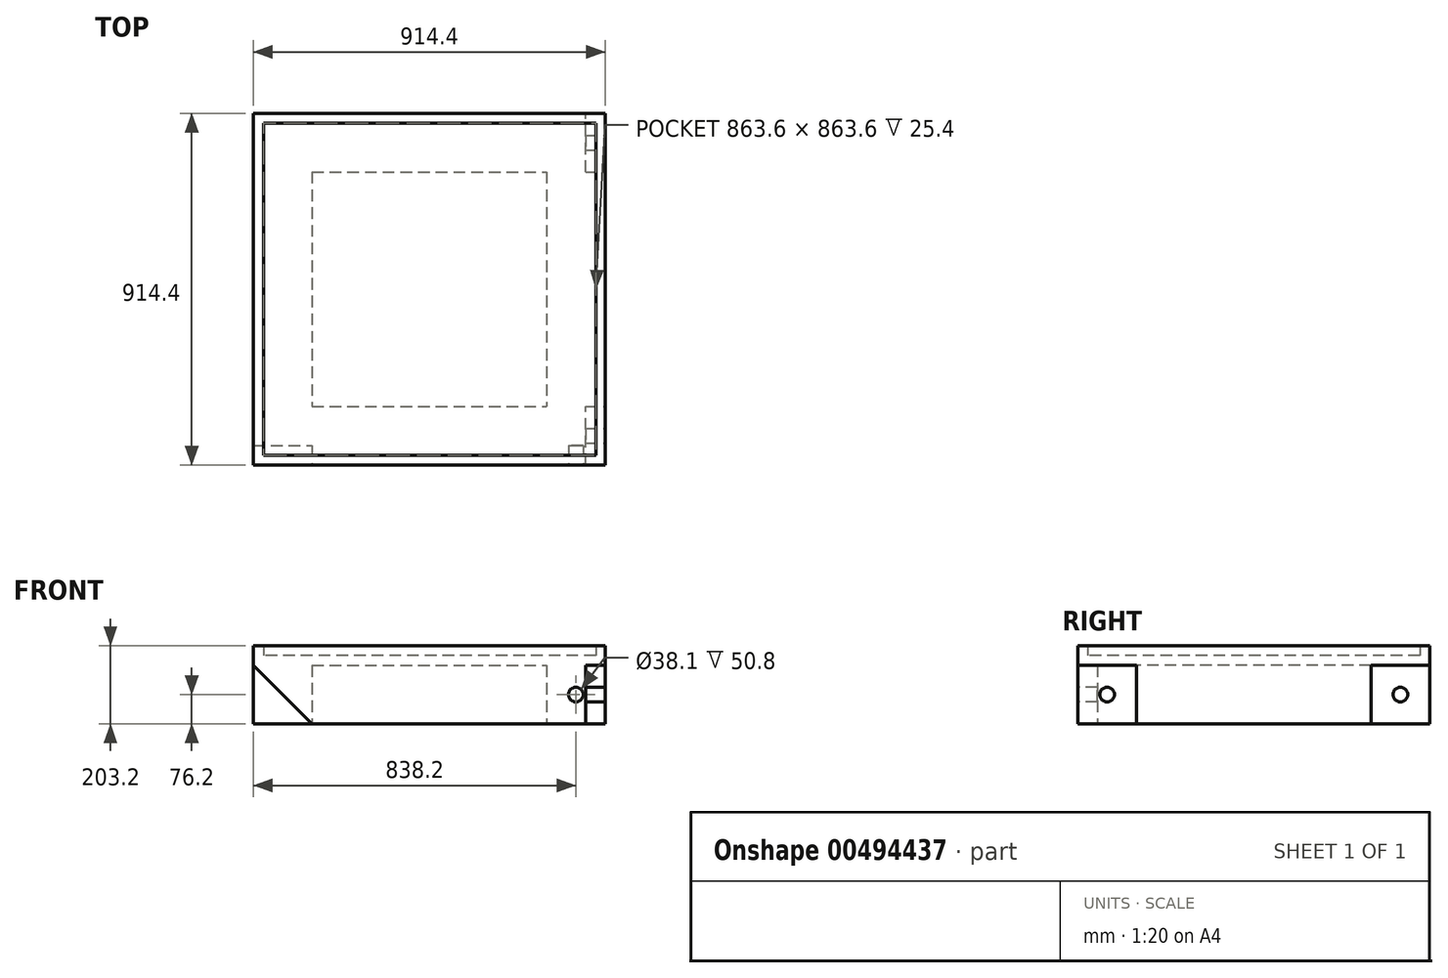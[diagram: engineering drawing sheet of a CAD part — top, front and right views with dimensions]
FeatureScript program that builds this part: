
annotation { "Feature Type Name" : "Feature", "Feature Type Description" : "" }
export const myFeature = defineFeature(function(context is Context, id is Id, definition is map)
    precondition{}
    {
        {
            var Q0;
            Q0=qCreatedBy(makeId("Top.planeOp"),FACE);
            var sketch = newSketch(context, id + "F0", { "sketchPlane" : qUnion([Q0])});
            skLineSegment(sketch, "E0.bottom", {"start": v(-458.1, -457.05) * mm, "end": v(456.3, -457.05) * mm});
            skLineSegment(sketch, "E0.top", {"start": v(-458.1, 457.35) * mm, "end": v(456.3, 457.35) * mm});
            skLineSegment(sketch, "E0.left", {"start": v(-458.1, -457.05) * mm, "end": v(-458.1, 457.35) * mm});
            skLineSegment(sketch, "E0.right", {"start": v(456.3, -457.05) * mm, "end": v(456.3, 457.35) * mm});
            skSolve(sketch);
        }
        {
            var Q0;
            Q0 = qSketchRegion(id + "F0", true);
            extrude(context, id + "F1", {"entities" : qUnion([Q0]), "depth" : 177.8 * mm});
        }
        {
            var Q0;
            Q0=makeQuery(id+"F1.opExtrude","CAP_FACE",FACE,{"disambiguationData":[OSD([sQuery(id+"F0.wireOp",EDGE,"E0.bottom"),sQuery(id+"F0.wireOp",EDGE,"E0.top"),sQuery(id+"F0.wireOp",EDGE,"E0.left"),sQuery(id+"F0.wireOp",EDGE,"E0.right")])],"isStart":true});
            var sketch = newSketch(context, id + "F2", { "sketchPlane" : qUnion([Q0])});
            skLineSegment(sketch, "E1.bottom", {"start": v(-458.1, 457.05) * mm, "end": v(-305.7, 457.05) * mm});
            skLineSegment(sketch, "E1.top", {"start": v(-458.1, 304.65) * mm, "end": v(-305.7, 304.65) * mm});
            skLineSegment(sketch, "E1.left", {"start": v(-458.1, 457.05) * mm, "end": v(-458.1, 304.65) * mm});
            skLineSegment(sketch, "E1.right", {"start": v(-305.7, 457.05) * mm, "end": v(-305.7, 304.65) * mm});
            skLineSegment(sketch, "E2.bottom", {"start": v(-458.1, -457.35) * mm, "end": v(-305.7, -457.35) * mm});
            skLineSegment(sketch, "E2.top", {"start": v(-458.1, -304.95) * mm, "end": v(-305.7, -304.95) * mm});
            skLineSegment(sketch, "E2.left", {"start": v(-458.1, -457.35) * mm, "end": v(-458.1, -304.95) * mm});
            skLineSegment(sketch, "E2.right", {"start": v(-305.7, -457.35) * mm, "end": v(-305.7, -304.95) * mm});
            skLineSegment(sketch, "E3.bottom", {"start": v(456.3, -457.35) * mm, "end": v(303.9, -457.35) * mm});
            skLineSegment(sketch, "E3.top", {"start": v(456.3, -304.95) * mm, "end": v(303.9, -304.95) * mm});
            skLineSegment(sketch, "E3.left", {"start": v(456.3, -457.35) * mm, "end": v(456.3, -304.95) * mm});
            skLineSegment(sketch, "E3.right", {"start": v(303.9, -457.35) * mm, "end": v(303.9, -304.95) * mm});
            skLineSegment(sketch, "E4.bottom", {"start": v(456.3, 457.05) * mm, "end": v(303.9, 457.05) * mm});
            skLineSegment(sketch, "E4.top", {"start": v(456.3, 304.65) * mm, "end": v(303.9, 304.65) * mm});
            skLineSegment(sketch, "E4.left", {"start": v(456.3, 457.05) * mm, "end": v(456.3, 304.65) * mm});
            skLineSegment(sketch, "E4.right", {"start": v(303.9, 457.05) * mm, "end": v(303.9, 304.65) * mm});
            skLineSegment(sketch, "E5.bottom", {"start": v(-305.7, -304.95) * mm, "end": v(303.9, -304.95) * mm});
            skLineSegment(sketch, "E5.top", {"start": v(-305.7, 304.65) * mm, "end": v(303.9, 304.65) * mm});
            skLineSegment(sketch, "E5.left", {"start": v(-305.7, -304.95) * mm, "end": v(-305.7, 304.65) * mm});
            skLineSegment(sketch, "E5.right", {"start": v(303.9, -304.95) * mm, "end": v(303.9, 304.65) * mm});
            skSolve(sketch);
        }
        {
            var Q0;
            Q0=makeQuery(id+"F2.imprint","IMPRINT",FACE,{"disambiguationData":[TD([[makeQuery(id+"F2.imprint","IMPRINT",EDGE,{"derivedFrom":sQuery(id+"F2.wireOp",EDGE,"E5.bottom")}),1.0]])]});
            extrude(context, id + "F3", {"entities" : qUnion([Q0]), "operationType" : NewBodyOperationType.REMOVE, "oppositeDirection" : true, "depth" : 152.4 * mm});
        }
        {
            var Q0;
            Q0=makeQuery(id+"F1.opExtrude","CAP_FACE",FACE,{"disambiguationData":[OSD([sQuery(id+"F0.wireOp",EDGE,"E0.bottom"),sQuery(id+"F0.wireOp",EDGE,"E0.top"),sQuery(id+"F0.wireOp",EDGE,"E0.left"),sQuery(id+"F0.wireOp",EDGE,"E0.right")])],"isStart":false});
            var sketch = newSketch(context, id + "F4", { "sketchPlane" : qUnion([Q0])});
            skSolve(sketch);
        }
        {
            var Q0;
            Q0=makeQuery(id+"F1.opExtrude","SWEPT_FACE",FACE,{"disambiguationData":[OSD([sQuery(id+"F0.wireOp",EDGE,"E0.bottom")])]});
            var sketch = newSketch(context, id + "F5", { "sketchPlane" : qUnion([Q0])});
            skLineSegment(sketch, "E6.bottom", {"start": v(456.3, 0) * mm, "end": v(303.9, 0) * mm});
            skLineSegment(sketch, "E6.top", {"start": v(456.3, 152.4) * mm, "end": v(303.9, 152.4) * mm});
            skLineSegment(sketch, "E6.left", {"start": v(456.3, 0) * mm, "end": v(456.3, 152.4) * mm});
            skLineSegment(sketch, "E6.right", {"start": v(303.9, 0) * mm, "end": v(303.9, 152.4) * mm});
            skLineSegment(sketch, "E7.bottom", {"start": v(-458.1, 0) * mm, "end": v(-305.7, 0) * mm});
            skLineSegment(sketch, "E7.top", {"start": v(-458.1, 152.4) * mm, "end": v(-305.7, 152.4) * mm});
            skLineSegment(sketch, "E7.left", {"start": v(-458.1, 0) * mm, "end": v(-458.1, 152.4) * mm});
            skLineSegment(sketch, "E7.right", {"start": v(-305.7, 0) * mm, "end": v(-305.7, 152.4) * mm});
            skLineSegment(sketch, "E8", {"start": v(303.9, 152.4) * mm, "end": v(456.3, 0) * mm});
            skLineSegment(sketch, "E9", {"start": v(456.3, 152.4) * mm, "end": v(303.9, 0) * mm});
            skLineSegment(sketch, "E10", {"start": v(-305.7, 152.4) * mm, "end": v(-458.1, 0) * mm});
            skLineSegment(sketch, "E11", {"start": v(-458.1, 152.4) * mm, "end": v(-305.7, 0) * mm});
            skCircle(sketch, "E12", {"center": v(-381.9, 76.2) * mm, "radius": 19.05 * mm});
            skCircle(sketch, "E13", {"center": v(380.1, 76.2) * mm, "radius": 19.05 * mm});
            skSolve(sketch);
        }
        {
            var Q0;
            {var subQ0=sQuery(id+"F5.wireOp",EDGE,"E9");var subQ1=sQuery(id+"F5.wireOp",EDGE,"E8");var subQ2=makeQuery(id+"F5.imprint","INTERSECT",VERTEX,{"derivedFrom":[subQ1,subQ0]});Q0=makeQuery(id+"F5.imprint","IMPRINT",FACE,{"disambiguationData":[TD([[makeQuery(id+"F5.imprint","IMPRINT",EDGE,{"disambiguationData":[TD([[subQ2,-1.0]])],"derivedFrom":subQ1}),1.0]])]});}
            var Q1;
            {var subQ0=sQuery(id+"F5.wireOp",EDGE,"E13");var subQ1=sQuery(id+"F5.wireOp",EDGE,"E8");var subQ2=makeQuery(id+"F5.imprint","INTERSECT",VERTEX,{"disambiguationData":[OD(0.0)],"derivedFrom":[subQ1,subQ0]});Q1=makeQuery(id+"F5.imprint","IMPRINT",FACE,{"disambiguationData":[TD([[makeQuery(id+"F5.imprint","IMPRINT",EDGE,{"disambiguationData":[TD([[subQ2,-1.0]])],"derivedFrom":subQ1}),1.0]])]});}
            var Q2;
            {var subQ0=sQuery(id+"F5.wireOp",EDGE,"E13");var subQ1=sQuery(id+"F5.wireOp",EDGE,"E8");var subQ2=makeQuery(id+"F5.imprint","INTERSECT",VERTEX,{"disambiguationData":[OD(0.0)],"derivedFrom":[subQ1,subQ0]});Q2=makeQuery(id+"F5.imprint","IMPRINT",FACE,{"disambiguationData":[TD([[makeQuery(id+"F5.imprint","IMPRINT",EDGE,{"disambiguationData":[TD([[subQ2,-1.0]])],"derivedFrom":subQ1}),-1.0]])]});}
            var Q3;
            {var subQ0=sQuery(id+"F5.wireOp",EDGE,"E9");var subQ1=sQuery(id+"F5.wireOp",EDGE,"E8");var subQ2=makeQuery(id+"F5.imprint","INTERSECT",VERTEX,{"derivedFrom":[subQ1,subQ0]});Q3=makeQuery(id+"F5.imprint","IMPRINT",FACE,{"disambiguationData":[TD([[makeQuery(id+"F5.imprint","IMPRINT",EDGE,{"disambiguationData":[TD([[subQ2,-1.0]])],"derivedFrom":subQ1}),-1.0]])]});}
            var Q4;
            {var subQ0=sQuery(id+"F5.wireOp",EDGE,"E12");var subQ1=sQuery(id+"F5.wireOp",EDGE,"E10");var subQ2=makeQuery(id+"F5.imprint","INTERSECT",VERTEX,{"disambiguationData":[OD(0.0)],"derivedFrom":[subQ1,subQ0]});Q4=makeQuery(id+"F5.imprint","IMPRINT",FACE,{"disambiguationData":[TD([[makeQuery(id+"F5.imprint","IMPRINT",EDGE,{"disambiguationData":[TD([[subQ2,-1.0]])],"derivedFrom":subQ1}),1.0]])]});}
            var Q5;
            {var subQ0=sQuery(id+"F5.wireOp",EDGE,"E12");var subQ1=sQuery(id+"F5.wireOp",EDGE,"E10");var subQ2=makeQuery(id+"F5.imprint","INTERSECT",VERTEX,{"disambiguationData":[OD(0.0)],"derivedFrom":[subQ1,subQ0]});Q5=makeQuery(id+"F5.imprint","IMPRINT",FACE,{"disambiguationData":[TD([[makeQuery(id+"F5.imprint","IMPRINT",EDGE,{"disambiguationData":[TD([[subQ2,-1.0]])],"derivedFrom":subQ1}),-1.0]])]});}
            var Q6;
            {var subQ0=sQuery(id+"F5.wireOp",EDGE,"E11");var subQ1=sQuery(id+"F5.wireOp",EDGE,"E10");var subQ2=makeQuery(id+"F5.imprint","INTERSECT",VERTEX,{"derivedFrom":[subQ1,subQ0]});Q6=makeQuery(id+"F5.imprint","IMPRINT",FACE,{"disambiguationData":[TD([[makeQuery(id+"F5.imprint","IMPRINT",EDGE,{"disambiguationData":[TD([[subQ2,-1.0]])],"derivedFrom":subQ1}),-1.0]])]});}
            var Q7;
            {var subQ0=sQuery(id+"F5.wireOp",EDGE,"E11");var subQ1=sQuery(id+"F5.wireOp",EDGE,"E10");var subQ2=makeQuery(id+"F5.imprint","INTERSECT",VERTEX,{"derivedFrom":[subQ1,subQ0]});Q7=makeQuery(id+"F5.imprint","IMPRINT",FACE,{"disambiguationData":[TD([[makeQuery(id+"F5.imprint","IMPRINT",EDGE,{"disambiguationData":[TD([[subQ2,-1.0]])],"derivedFrom":subQ1}),1.0]])]});}
            extrude(context, id + "F6", {"entities" : qUnion([Q0, Q1, Q2, Q3, Q4, Q5, Q6, Q7]), "operationType" : NewBodyOperationType.REMOVE, "oppositeDirection" : true, "depth" : 50.8 * mm});
        }
        {
            var Q0;
            Q0=makeQuery(id+"F1.opExtrude","SWEPT_FACE",FACE,{"disambiguationData":[OSD([sQuery(id+"F0.wireOp",EDGE,"E0.right")])]});
            var sketch = newSketch(context, id + "F7", { "sketchPlane" : qUnion([Q0])});
            skLineSegment(sketch, "E14.bottom", {"start": v(-457.05, 0) * mm, "end": v(-304.65, 0) * mm});
            skLineSegment(sketch, "E14.top", {"start": v(-457.05, 152.4) * mm, "end": v(-304.65, 152.4) * mm});
            skLineSegment(sketch, "E14.left", {"start": v(-457.05, 0) * mm, "end": v(-457.05, 152.4) * mm});
            skLineSegment(sketch, "E14.right", {"start": v(-304.65, 0) * mm, "end": v(-304.65, 152.4) * mm});
            skLineSegment(sketch, "E15.bottom", {"start": v(457.35, 0) * mm, "end": v(304.95, 0) * mm});
            skLineSegment(sketch, "E15.top", {"start": v(457.35, 152.4) * mm, "end": v(304.95, 152.4) * mm});
            skLineSegment(sketch, "E15.left", {"start": v(457.35, 0) * mm, "end": v(457.35, 152.4) * mm});
            skLineSegment(sketch, "E15.right", {"start": v(304.95, 0) * mm, "end": v(304.95, 152.4) * mm});
            skLineSegment(sketch, "E16", {"start": v(-457.05, 152.4) * mm, "end": v(-304.65, 0) * mm});
            skLineSegment(sketch, "E17", {"start": v(457.35, 152.4) * mm, "end": v(304.95, 0) * mm});
            skCircle(sketch, "E18", {"center": v(-380.85, 76.2) * mm, "radius": 19.05 * mm});
            skCircle(sketch, "E19", {"center": v(381.15, 76.2) * mm, "radius": 19.05 * mm});
            skSolve(sketch);
        }
        {
            var Q0;
            {var subQ0=sQuery(id+"F7.wireOp",EDGE,"E19");var subQ1=sQuery(id+"F7.wireOp",EDGE,"E17");var subQ2=makeQuery(id+"F7.imprint","INTERSECT",VERTEX,{"disambiguationData":[OD(0.0)],"derivedFrom":[subQ1,subQ0]});Q0=makeQuery(id+"F7.imprint","IMPRINT",FACE,{"disambiguationData":[TD([[makeQuery(id+"F7.imprint","IMPRINT",EDGE,{"disambiguationData":[TD([[subQ2,-1.0]])],"derivedFrom":subQ1}),1.0]])]});}
            var Q1;
            {var subQ0=sQuery(id+"F7.wireOp",EDGE,"E19");var subQ1=sQuery(id+"F7.wireOp",EDGE,"E17");var subQ2=makeQuery(id+"F7.imprint","INTERSECT",VERTEX,{"disambiguationData":[OD(0.0)],"derivedFrom":[subQ1,subQ0]});Q1=makeQuery(id+"F7.imprint","IMPRINT",FACE,{"disambiguationData":[TD([[makeQuery(id+"F7.imprint","IMPRINT",EDGE,{"disambiguationData":[TD([[subQ2,-1.0]])],"derivedFrom":subQ1}),-1.0]])]});}
            var Q2;
            {var subQ0=sQuery(id+"F7.wireOp",EDGE,"E18");var subQ1=sQuery(id+"F7.wireOp",EDGE,"E16");var subQ2=makeQuery(id+"F7.imprint","INTERSECT",VERTEX,{"disambiguationData":[OD(0.0)],"derivedFrom":[subQ1,subQ0]});Q2=makeQuery(id+"F7.imprint","IMPRINT",FACE,{"disambiguationData":[TD([[makeQuery(id+"F7.imprint","IMPRINT",EDGE,{"disambiguationData":[TD([[subQ2,-1.0]])],"derivedFrom":subQ1}),1.0]])]});}
            var Q3;
            {var subQ0=sQuery(id+"F7.wireOp",EDGE,"E18");var subQ1=sQuery(id+"F7.wireOp",EDGE,"E16");var subQ2=makeQuery(id+"F7.imprint","INTERSECT",VERTEX,{"disambiguationData":[OD(0.0)],"derivedFrom":[subQ1,subQ0]});Q3=makeQuery(id+"F7.imprint","IMPRINT",FACE,{"disambiguationData":[TD([[makeQuery(id+"F7.imprint","IMPRINT",EDGE,{"disambiguationData":[TD([[subQ2,-1.0]])],"derivedFrom":subQ1}),-1.0]])]});}
            extrude(context, id + "F8", {"entities" : qUnion([Q0, Q1, Q2, Q3]), "operationType" : NewBodyOperationType.REMOVE, "oppositeDirection" : true, "depth" : 50.8 * mm});
        }
        {
            var Q0;
            Q0=makeQuery(id+"F4.imprint","IMPRINT",FACE,{"disambiguationData":[TD([[makeQuery(id+"F4.imprint","IMPRINT",EDGE,{"derivedFrom":makeQuery(id+"F1.opExtrude","CAP_EDGE",EDGE,{"disambiguationData":[OSD([sQuery(id+"F0.wireOp",EDGE,"E0.bottom")])],"isStart":false})}),1.0]])]});
            var sketch = newSketch(context, id + "F9", { "sketchPlane" : qUnion([Q0])});
            skLineSegment(sketch, "E20.bottom", {"start": v(431.8, 431.8) * mm, "end": v(-431.8, 431.8) * mm});
            skLineSegment(sketch, "E20.top", {"start": v(431.8, -431.8) * mm, "end": v(-431.8, -431.8) * mm});
            skLineSegment(sketch, "E20.left", {"start": v(431.8, 431.8) * mm, "end": v(431.8, -431.8) * mm});
            skLineSegment(sketch, "E20.right", {"start": v(-431.8, 431.8) * mm, "end": v(-431.8, -431.8) * mm});
            skPoint(sketch, "E20.middle", {"position": v(0, 0) * mm});
            skSolve(sketch);
        }
        {
            var Q0;
            Q0=makeQuery(id+"F9.imprint","IMPRINT",FACE,{"disambiguationData":[TD([[makeQuery(id+"F9.imprint","IMPRINT",EDGE,{"derivedFrom":sQuery(id+"F9.wireOp",EDGE,"E20.bottom")}),-1.0]])]});
            extrude(context, id + "F10", {"entities" : qUnion([Q0]), "operationType" : NewBodyOperationType.ADD, "depth" : 25.4 * mm});
        }
    });
